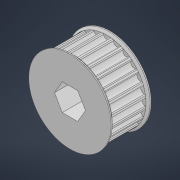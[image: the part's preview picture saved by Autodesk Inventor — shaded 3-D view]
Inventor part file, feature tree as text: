
AUTODESK INVENTOR PART (.ipt)
format: ipt  version: 2021 (Build 250183000, 183)  size: 306,176 bytes
history: native  units: in
note: dims shown in document units (in); Inventor stores cm internally (conversion verified against a paired STEP export)
features: extrude x7, sketch x7, fillet x2, pattern_circular x2, mirror x2, chamfer x2, other x1
ambient origin geometry x8: Origin, YZ Plane, XZ Plane, XY Plane, X Axis, Y Axis, Z Axis, Center Point
bodies: Solid1 (feature_tree)
feature tree (23):
  other  "Hex Bore"
  extrude  "HTD Base"  Depth=0.6299in TaperAngle=0.0deg
  extrude  "HTD Base Tooth"  Depth=0.0113in
  fillet  "HTD Base Tooth pt. 2"  [1 undecoded]
  pattern_circular  "HTD Teeth"  Count=24  [1 undecoded]
  extrude  "HTD Flange"  Depth=0.0394in
  mirror  "HTD Flanges"
  chamfer  "HTD Flange Chamfer"  Distance=0.0787in Angle=45.0deg
  extrude  "GT2 Base"  Depth=0.5in
  extrude  "GT2 Base Tooth"  TaperAngle=0.0deg  [1 undecoded]
  fillet  "GT2 Base Tooth pt. 2"  Radius=0.5in
  pattern_circular  "GT2 Teeth"  [2 undecoded]
  extrude  "GT2 Flange"  Depth=0.0591in
  mirror  "GT2 Flanges"
  chamfer  "GT2 Flange Chamfer"  Distance=0.6299in
  extrude  "Circle Bore"  TaperAngle=0.0deg  [1 undecoded]
  sketch  "Sketch1"  dims[d0=1.4588in d1=0.6299in d2=0.0in]
  sketch  "Sketch2"  dims[d3=0.1208in d5=0.0113in d6=0.0in d7=0.0in]
  sketch  "Sketch4"  dims[d8=0.0169in d9=9.4488in]
  sketch  "Sketch5"  dims[d10=360.0deg d12=0.0394in]
  sketch  "Sketch6"  dims[d13=0.0591in]
  sketch  "Sketch7"  dims[d14=0.0in]
  sketch  "Sketch8"  dims[d15=0.0394in d16=0.0787in d17=45.0deg d18=0.5in d19=0.0in d20=0.0in d21=0.5in d22=0.0in d23=0.0in d24=0.8723in d25=0.6299in d26=0.0in d27=0.0727in d28=0.0075in d29=0.0in d30=0.0in d31=0.0118in d32=9.4488in d33=360.0deg d35=0.0394in d36=0.0591in d37=0.0in d38=0.0394in d39=0.0787in d40=45.0deg]
note: 6 required parameter values undecoded (feature->parameter linkage not recoverable at this tier; creation-order binding heuristic only, values carry confidence <= 0.55)
